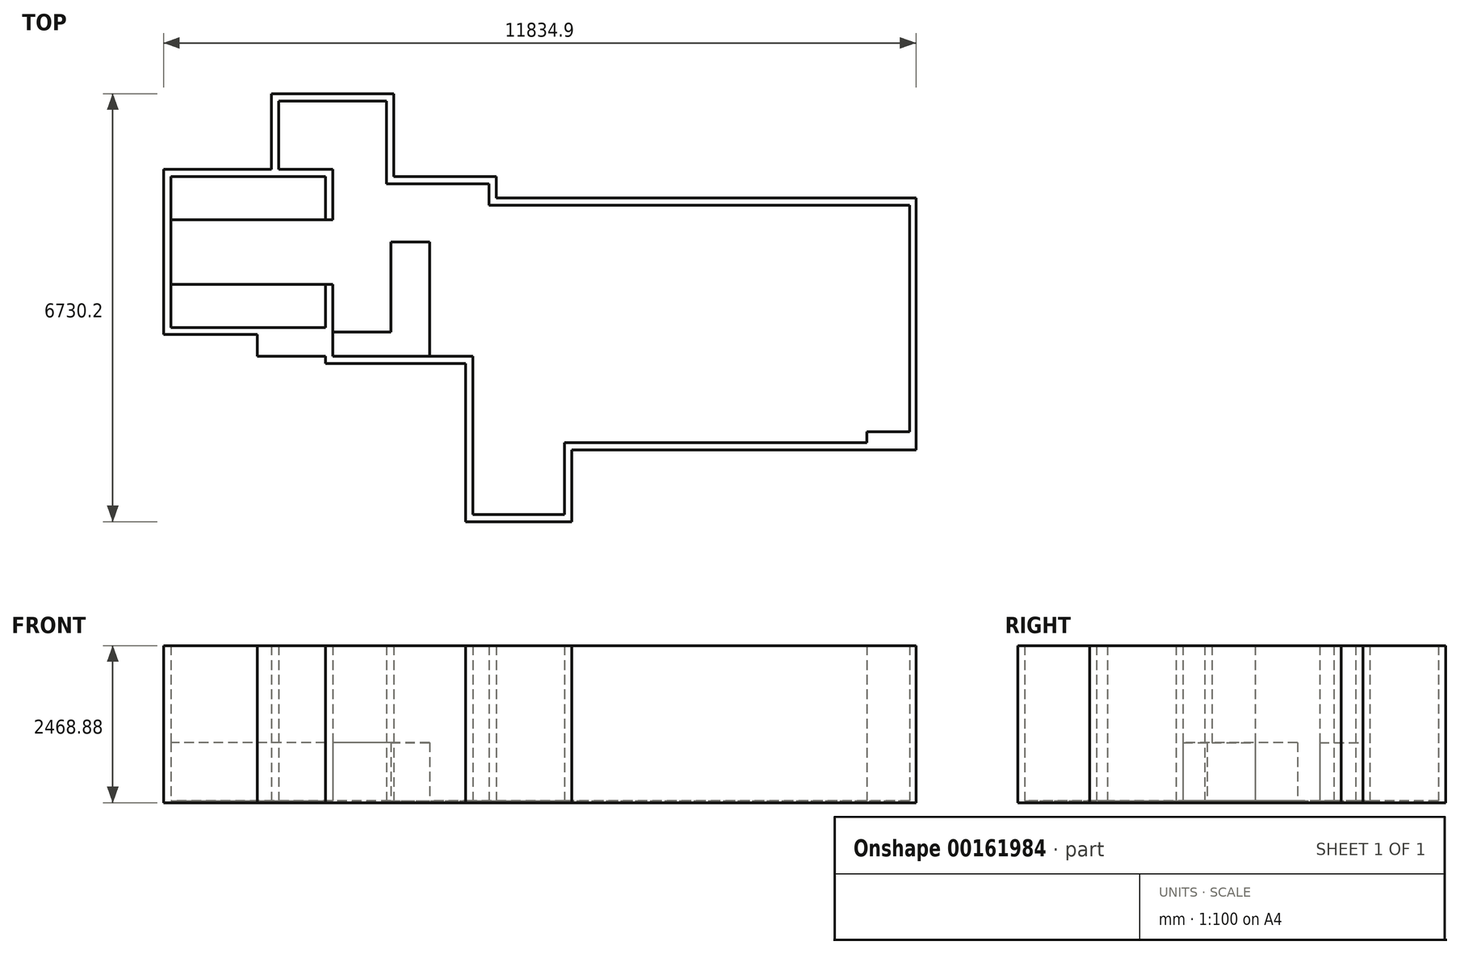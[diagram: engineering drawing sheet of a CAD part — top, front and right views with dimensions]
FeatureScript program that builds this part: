
annotation { "Feature Type Name" : "Feature", "Feature Type Description" : "" }
export const myFeature = defineFeature(function(context is Context, id is Id, definition is map)
    precondition{}
    {
        {
            var Q0;
            Q0=qCreatedBy(makeId("Top.planeOp"),FACE);
            var sketch = newSketch(context, id + "F0", { "sketchPlane" : qUnion([Q0])});
            skLineSegment(sketch, "E0", {"start": v(0, 0) * mm, "end": v(-2206.14, 0) * mm});
            skLineSegment(sketch, "E1", {"start": v(-3054.7, 2940.2) * mm, "end": v(-3054.7, 4014.92) * mm});
            skLineSegment(sketch, "E2", {"start": v(-3054.7, 4014.92) * mm, "end": v(-1357.58, 4014.92) * mm});
            skLineSegment(sketch, "E3", {"start": v(-1357.58, 4014.92) * mm, "end": v(-1357.58, 2714.04) * mm});
            skLineSegment(sketch, "E4", {"start": v(-1357.58, 2714.04) * mm, "end": v(254.74, 2714.04) * mm});
            skLineSegment(sketch, "E5", {"start": v(254.74, 2714.04) * mm, "end": v(254.74, 2374.61) * mm});
            skLineSegment(sketch, "E6", {"start": v(254.74, 2374.61) * mm, "end": v(6873.47, 2374.61) * mm});
            skLineSegment(sketch, "E7", {"start": v(6873.47, 2374.61) * mm, "end": v(6873.47, -1189.47) * mm});
            skLineSegment(sketch, "E8", {"start": v(1442.58, -2489) * mm, "end": v(0, -2489) * mm});
            skLineSegment(sketch, "E9", {"start": v(0, -2489) * mm, "end": v(0, 0) * mm});
            skLineSegment(sketch, "E10", {"start": v(-2206.14, 0) * mm, "end": v(-2206.14, 1131.45) * mm});
            skLineSegment(sketch, "E11", {"start": v(-2206.14, 1131.45) * mm, "end": v(-2319.29, 1131.45) * mm});
            skLineSegment(sketch, "E12", {"start": v(-2319.29, 1131.45) * mm, "end": v(-2319.29, 452.66) * mm});
            skLineSegment(sketch, "E13", {"start": v(-2319.29, 452.66) * mm, "end": v(-4751.6, 452.66) * mm});
            skLineSegment(sketch, "E14", {"start": v(-4751.6, 452.66) * mm, "end": v(-4751.6, 2827.06) * mm});
            skLineSegment(sketch, "E15", {"start": v(-4751.6, 2827.06) * mm, "end": v(-2319.29, 2827.06) * mm});
            skLineSegment(sketch, "E16", {"start": v(-2319.29, 2827.06) * mm, "end": v(-2319.29, 2148.27) * mm});
            skLineSegment(sketch, "E17", {"start": v(-2319.29, 2148.27) * mm, "end": v(-2206.15, 2148.27) * mm});
            skLineSegment(sketch, "E18", {"start": v(-2206.15, 2148.27) * mm, "end": v(-2206.15, 2940.2) * mm});
            skLineSegment(sketch, "E19", {"start": v(-2206.15, 2940.2) * mm, "end": v(-4864.73, 2940.2) * mm});
            skLineSegment(sketch, "E20", {"start": v(-2206.14, 0) * mm, "end": v(-3393.95, 0) * mm});
            skLineSegment(sketch, "E21", {"start": v(-3393.95, 0) * mm, "end": v(-3393.95, 339.52) * mm});
            skLineSegment(sketch, "E22", {"start": v(-3393.95, 339.52) * mm, "end": v(-4864.73, 339.52) * mm});
            skLineSegment(sketch, "E23", {"start": v(-4864.73, 2940.2) * mm, "end": v(-4864.73, 339.52) * mm});
            skLineSegment(sketch, "E24", {"start": v(-2319.29, 1131.45) * mm, "end": v(-4751.6, 1131.45) * mm});
            skLineSegment(sketch, "E25", {"start": v(-2319.29, 2148.27) * mm, "end": v(-4751.6, 2148.27) * mm});
            skLineSegment(sketch, "E26", {"start": v(6873.47, -1189.47) * mm, "end": v(6194.68, -1189.47) * mm});
            skLineSegment(sketch, "E27", {"start": v(6194.68, -1189.47) * mm, "end": v(6194.68, -1359.18) * mm});
            skLineSegment(sketch, "E28", {"start": v(6194.68, -1359.18) * mm, "end": v(1442.58, -1359.18) * mm});
            skLineSegment(sketch, "E29", {"start": v(1442.58, -1359.18) * mm, "end": v(1442.58, -2489) * mm});
            skLineSegment(sketch, "E30", {"start": v(-2319.29, 0) * mm, "end": v(-2319.29, -113.14) * mm});
            skLineSegment(sketch, "E31", {"start": v(-2319.29, -113.14) * mm, "end": v(-113.14, -113.14) * mm});
            skLineSegment(sketch, "E32", {"start": v(-113.14, -113.14) * mm, "end": v(-113.14, -2602.14) * mm});
            skLineSegment(sketch, "E33", {"start": v(-113.14, -2602.14) * mm, "end": v(1555.72, -2602.14) * mm});
            skLineSegment(sketch, "E34", {"start": v(1555.72, -2602.14) * mm, "end": v(1555.72, -1472.32) * mm});
            skLineSegment(sketch, "E35", {"start": v(1555.72, -1472.32) * mm, "end": v(6980.94, -1472.32) * mm});
            skLineSegment(sketch, "E36", {"start": v(6980.94, -1472.32) * mm, "end": v(6980.94, -1472.32) * mm});
            skLineSegment(sketch, "E37", {"start": v(6970.15, -1472.32) * mm, "end": v(6970.15, 2487.75) * mm});
            skLineSegment(sketch, "E38", {"start": v(6970.15, 2487.75) * mm, "end": v(367.88, 2487.75) * mm});
            skLineSegment(sketch, "E39", {"start": v(367.88, 2487.75) * mm, "end": v(367.88, 2827.18) * mm});
            skLineSegment(sketch, "E40", {"start": v(367.88, 2827.18) * mm, "end": v(-1244.44, 2827.18) * mm});
            skLineSegment(sketch, "E41", {"start": v(-1244.44, 2827.18) * mm, "end": v(-1244.44, 4128.06) * mm});
            skLineSegment(sketch, "E42", {"start": v(-1244.44, 4128.06) * mm, "end": v(-3167.85, 4128.06) * mm});
            skLineSegment(sketch, "E43", {"start": v(-3167.85, 4128.06) * mm, "end": v(-3167.85, 2940.2) * mm});
            skSolve(sketch);
        }
        {
            var Q0;
            Q0 = qSketchRegion(id + "F0", true);
            extrude(context, id + "F1", {"entities" : qUnion([Q0]), "depth" : 2438.4 * mm});
        }
        {
            var Q0;
            Q0=makeQuery(id+"F1.opExtrude","CAP_FACE",FACE,{"disambiguationData":[OSD([sQuery(id+"F0.wireOp",EDGE,"E0"),sQuery(id+"F0.wireOp",EDGE,"E1"),sQuery(id+"F0.wireOp",EDGE,"E2"),sQuery(id+"F0.wireOp",EDGE,"E3"),sQuery(id+"F0.wireOp",EDGE,"E4"),sQuery(id+"F0.wireOp",EDGE,"E5"),sQuery(id+"F0.wireOp",EDGE,"E6"),sQuery(id+"F0.wireOp",EDGE,"E7"),sQuery(id+"F0.wireOp",EDGE,"E8"),sQuery(id+"F0.wireOp",EDGE,"E9"),sQuery(id+"F0.wireOp",EDGE,"E10"),sQuery(id+"F0.wireOp",EDGE,"E11"),sQuery(id+"F0.wireOp",EDGE,"E12"),sQuery(id+"F0.wireOp",EDGE,"E13"),sQuery(id+"F0.wireOp",EDGE,"E14"),sQuery(id+"F0.wireOp",EDGE,"E15"),sQuery(id+"F0.wireOp",EDGE,"E16"),sQuery(id+"F0.wireOp",EDGE,"E17"),sQuery(id+"F0.wireOp",EDGE,"E18"),sQuery(id+"F0.wireOp",EDGE,"E19"),sQuery(id+"F0.wireOp",EDGE,"E20"),sQuery(id+"F0.wireOp",EDGE,"E21"),sQuery(id+"F0.wireOp",EDGE,"E22"),sQuery(id+"F0.wireOp",EDGE,"E23"),sQuery(id+"F0.wireOp",EDGE,"E26"),sQuery(id+"F0.wireOp",EDGE,"E27"),sQuery(id+"F0.wireOp",EDGE,"E28"),sQuery(id+"F0.wireOp",EDGE,"E29"),sQuery(id+"F0.wireOp",EDGE,"E30"),sQuery(id+"F0.wireOp",EDGE,"E31"),sQuery(id+"F0.wireOp",EDGE,"E32"),sQuery(id+"F0.wireOp",EDGE,"E33"),sQuery(id+"F0.wireOp",EDGE,"E34"),sQuery(id+"F0.wireOp",EDGE,"E35"),sQuery(id+"F0.wireOp",EDGE,"E37"),sQuery(id+"F0.wireOp",EDGE,"E38"),sQuery(id+"F0.wireOp",EDGE,"E39"),sQuery(id+"F0.wireOp",EDGE,"E40"),sQuery(id+"F0.wireOp",EDGE,"E41"),sQuery(id+"F0.wireOp",EDGE,"E42"),sQuery(id+"F0.wireOp",EDGE,"E43")])],"isStart":true});
            var sketch = newSketch(context, id + "F2", { "sketchPlane" : qUnion([Q0])});
            skLineSegment(sketch, "E44", {"start": v(-3393.95, 0) * mm, "end": v(-3393.95, -339.52) * mm});
            skLineSegment(sketch, "E45", {"start": v(-3393.95, -339.52) * mm, "end": v(-4864.73, -339.52) * mm});
            skLineSegment(sketch, "E46", {"start": v(-4864.73, -339.52) * mm, "end": v(-4864.73, -2940.2) * mm});
            skLineSegment(sketch, "E47", {"start": v(-4864.73, -2940.2) * mm, "end": v(-3167.85, -2940.2) * mm});
            skLineSegment(sketch, "E48", {"start": v(-3167.85, -2940.2) * mm, "end": v(-3167.85, -4128.06) * mm});
            skLineSegment(sketch, "E49", {"start": v(-3167.85, -4128.06) * mm, "end": v(-1244.44, -4128.06) * mm});
            skLineSegment(sketch, "E50", {"start": v(-1244.44, -4128.06) * mm, "end": v(-1244.44, -2827.18) * mm});
            skLineSegment(sketch, "E51", {"start": v(-1244.44, -2827.18) * mm, "end": v(367.88, -2827.18) * mm});
            skLineSegment(sketch, "E52", {"start": v(367.88, -2827.18) * mm, "end": v(367.88, -2487.75) * mm});
            skLineSegment(sketch, "E53", {"start": v(367.88, -2487.75) * mm, "end": v(6970.15, -2487.75) * mm});
            skLineSegment(sketch, "E54", {"start": v(6970.15, -2487.75) * mm, "end": v(6970.15, 1472.32) * mm});
            skLineSegment(sketch, "E55", {"start": v(6970.15, 1472.32) * mm, "end": v(1555.72, 1472.32) * mm});
            skLineSegment(sketch, "E56", {"start": v(1555.72, 1472.32) * mm, "end": v(1555.72, 2602.14) * mm});
            skLineSegment(sketch, "E57", {"start": v(1555.72, 2602.14) * mm, "end": v(-113.14, 2602.14) * mm});
            skLineSegment(sketch, "E58", {"start": v(-113.14, 2602.14) * mm, "end": v(-113.14, 113.14) * mm});
            skLineSegment(sketch, "E59", {"start": v(-113.14, 113.14) * mm, "end": v(-2319.29, 113.14) * mm});
            skLineSegment(sketch, "E60", {"start": v(-2319.29, 113.14) * mm, "end": v(-2319.29, 0) * mm});
            skLineSegment(sketch, "E61", {"start": v(-2319.29, 0) * mm, "end": v(-3393.95, 0) * mm});
            skSolve(sketch);
        }
        {
            var Q0;
            Q0 = qSketchRegion(id + "F2", true);
            extrude(context, id + "F3", {"entities" : qUnion([Q0]), "operationType" : NewBodyOperationType.ADD, "depth" : 30.48 * mm});
        }
        {
            var Q0;
            Q0=makeQuery(id+"F3.opExtrude","CAP_FACE",FACE,{"disambiguationData":[OSD([sQuery(id+"F2.wireOp",EDGE,"E44"),sQuery(id+"F2.wireOp",EDGE,"E45"),sQuery(id+"F2.wireOp",EDGE,"E46"),sQuery(id+"F2.wireOp",EDGE,"E47"),sQuery(id+"F2.wireOp",EDGE,"E48"),sQuery(id+"F2.wireOp",EDGE,"E49"),sQuery(id+"F2.wireOp",EDGE,"E50"),sQuery(id+"F2.wireOp",EDGE,"E51"),sQuery(id+"F2.wireOp",EDGE,"E52"),sQuery(id+"F2.wireOp",EDGE,"E53"),sQuery(id+"F2.wireOp",EDGE,"E54"),sQuery(id+"F2.wireOp",EDGE,"E55"),sQuery(id+"F2.wireOp",EDGE,"E56"),sQuery(id+"F2.wireOp",EDGE,"E57"),sQuery(id+"F2.wireOp",EDGE,"E58"),sQuery(id+"F2.wireOp",EDGE,"E59"),sQuery(id+"F2.wireOp",EDGE,"E60"),sQuery(id+"F2.wireOp",EDGE,"E61")])],"isStart":true});
            var sketch = newSketch(context, id + "F4", { "sketchPlane" : qUnion([Q0])});
            skLineSegment(sketch, "E62.bottom", {"start": v(-2319.29, 1131.45) * mm, "end": v(-4751.6, 1131.45) * mm});
            skLineSegment(sketch, "E62.top", {"start": v(-2319.29, 452.66) * mm, "end": v(-4751.6, 452.66) * mm});
            skLineSegment(sketch, "E62.left", {"start": v(-2319.29, 1131.45) * mm, "end": v(-2319.29, 452.66) * mm});
            skLineSegment(sketch, "E62.right", {"start": v(-4751.6, 1131.45) * mm, "end": v(-4751.6, 452.66) * mm});
            skLineSegment(sketch, "E63.bottom", {"start": v(-2319.29, 2148.27) * mm, "end": v(-4751.6, 2148.27) * mm});
            skLineSegment(sketch, "E63.top", {"start": v(-2319.29, 2827.06) * mm, "end": v(-4751.6, 2827.06) * mm});
            skLineSegment(sketch, "E63.left", {"start": v(-2319.29, 2148.27) * mm, "end": v(-2319.29, 2827.06) * mm});
            skLineSegment(sketch, "E63.right", {"start": v(-4751.6, 2148.27) * mm, "end": v(-4751.6, 2827.06) * mm});
            skSolve(sketch);
        }
        {
            var Q0;
            Q0 = qSketchRegion(id + "F4", true);
            extrude(context, id + "F5", {"entities" : qUnion([Q0]), "operationType" : NewBodyOperationType.ADD, "depth" : 914.4 * mm});
        }
        {
            var Q0;
            Q0=makeQuery(id+"F3.opExtrude","CAP_FACE",FACE,{"disambiguationData":[OSD([sQuery(id+"F2.wireOp",EDGE,"E44"),sQuery(id+"F2.wireOp",EDGE,"E45"),sQuery(id+"F2.wireOp",EDGE,"E46"),sQuery(id+"F2.wireOp",EDGE,"E47"),sQuery(id+"F2.wireOp",EDGE,"E48"),sQuery(id+"F2.wireOp",EDGE,"E49"),sQuery(id+"F2.wireOp",EDGE,"E50"),sQuery(id+"F2.wireOp",EDGE,"E51"),sQuery(id+"F2.wireOp",EDGE,"E52"),sQuery(id+"F2.wireOp",EDGE,"E53"),sQuery(id+"F2.wireOp",EDGE,"E54"),sQuery(id+"F2.wireOp",EDGE,"E55"),sQuery(id+"F2.wireOp",EDGE,"E56"),sQuery(id+"F2.wireOp",EDGE,"E57"),sQuery(id+"F2.wireOp",EDGE,"E58"),sQuery(id+"F2.wireOp",EDGE,"E59"),sQuery(id+"F2.wireOp",EDGE,"E60"),sQuery(id+"F2.wireOp",EDGE,"E61")])],"isStart":true});
            var sketch = newSketch(context, id + "F6", { "sketchPlane" : qUnion([Q0])});
            skLineSegment(sketch, "E64.bottom", {"start": v(-1291.74, 1799.64) * mm, "end": v(-682.14, 1799.64) * mm});
            skLineSegment(sketch, "E64.left", {"start": v(-1291.74, 1799.64) * mm, "end": v(-1291.74, 379.27) * mm});
            skLineSegment(sketch, "E64.right", {"start": v(-682.14, 1799.64) * mm, "end": v(-682.14, 0) * mm});
            skLineSegment(sketch, "E65", {"start": v(-1291.74, 379.27) * mm, "end": v(-2206.14, 379.27) * mm});
            skLineSegment(sketch, "E66", {"start": v(-2206.14, 379.27) * mm, "end": v(-2206.14, 0) * mm});
            skLineSegment(sketch, "E67", {"start": v(-2206.14, 0) * mm, "end": v(-682.14, 0) * mm});
            skSolve(sketch);
        }
        {
            var Q0;
            Q0 = qSketchRegion(id + "F6", true);
            extrude(context, id + "F7", {"entities" : qUnion([Q0]), "operationType" : NewBodyOperationType.ADD, "depth" : 914.4 * mm});
        }
    });
